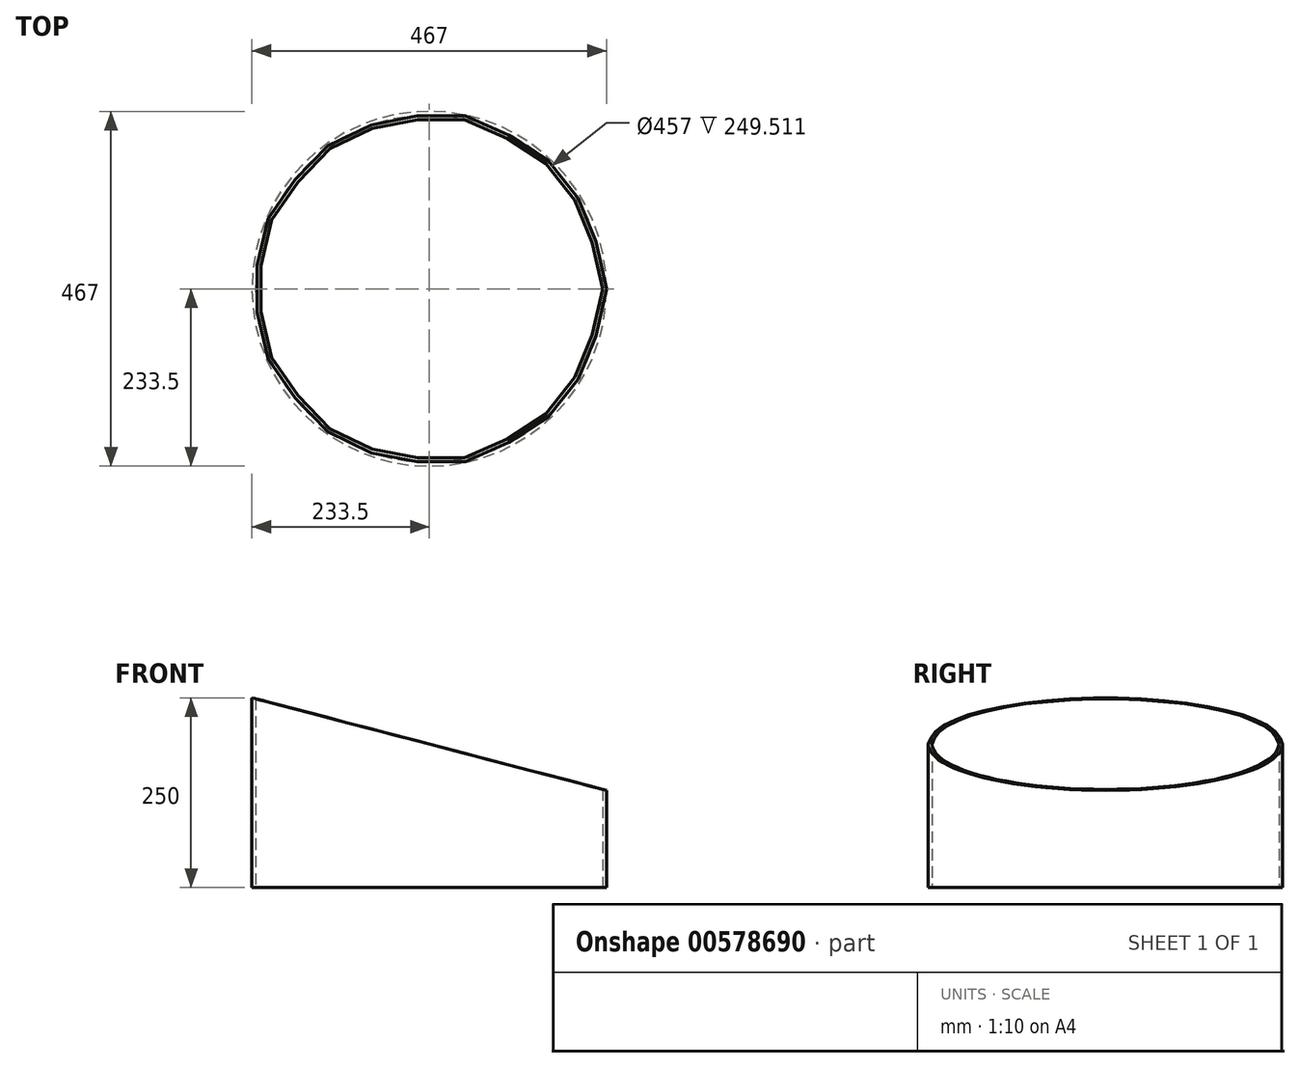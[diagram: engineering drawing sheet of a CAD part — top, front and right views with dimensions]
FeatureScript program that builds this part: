
annotation { "Feature Type Name" : "Feature", "Feature Type Description" : "" }
export const myFeature = defineFeature(function(context is Context, id is Id, definition is map)
    precondition{}
    {
        {
            var Q0;
            Q0=qCreatedBy(makeId("Top.planeOp"),FACE);
            var sketch = newSketch(context, id + "F0", { "sketchPlane" : qUnion([Q0])});
            skCircle(sketch, "E0", {"center": v(0, 0) * mm, "radius": 228.5 * mm});
            skCircle(sketch, "E1.0", {"center": v(0, 0) * mm, "radius": 233.5 * mm});
            skSolve(sketch);
        }
        {
            var Q0;
            Q0=makeQuery(id+"F0.imprint","IMPRINT",FACE,{"disambiguationData":[TD([[makeQuery(id+"F0.imprint","IMPRINT",EDGE,{"derivedFrom":sQuery(id+"F0.wireOp",EDGE,"E0")}),-1.0]])]});
            extrude(context, id + "F1", {"entities" : qUnion([Q0]), "depth" : 250 * mm, "offsetDistance" : 25 * mm});
        }
        {
            var Q0;
            Q0=qCreatedBy(makeId("Front.planeOp"),FACE);
            var sketch = newSketch(context, id + "F2", { "sketchPlane" : qUnion([Q0])});
            skLineSegment(sketch, "E2", {"start": v(233.5, 250) * mm, "end": v(233.5, 128) * mm});
            skLineSegment(sketch, "E3", {"start": v(-233.5, 250) * mm, "end": v(233.5, 128) * mm});
            skLineSegment(sketch, "E4.0", {"start": v(-233.5, 250) * mm, "end": v(233.5, 250) * mm});
            skSolve(sketch);
        }
        {
            var Q0;
            Q0=makeQuery(id+"F2.imprint","IMPRINT",FACE,{"disambiguationData":[TD([[makeQuery(id+"F2.imprint","IMPRINT",EDGE,{"derivedFrom":sQuery(id+"F2.wireOp",EDGE,"E2")}),-1.0]])]});
            extrude(context, id + "F3", {"entities" : qUnion([Q0]), "operationType" : NewBodyOperationType.REMOVE, "endBound" : BoundingType.SYMMETRIC, "oppositeDirection" : true, "depth" : 475 * mm, "offsetDistance" : 25 * mm});
        }
    });
